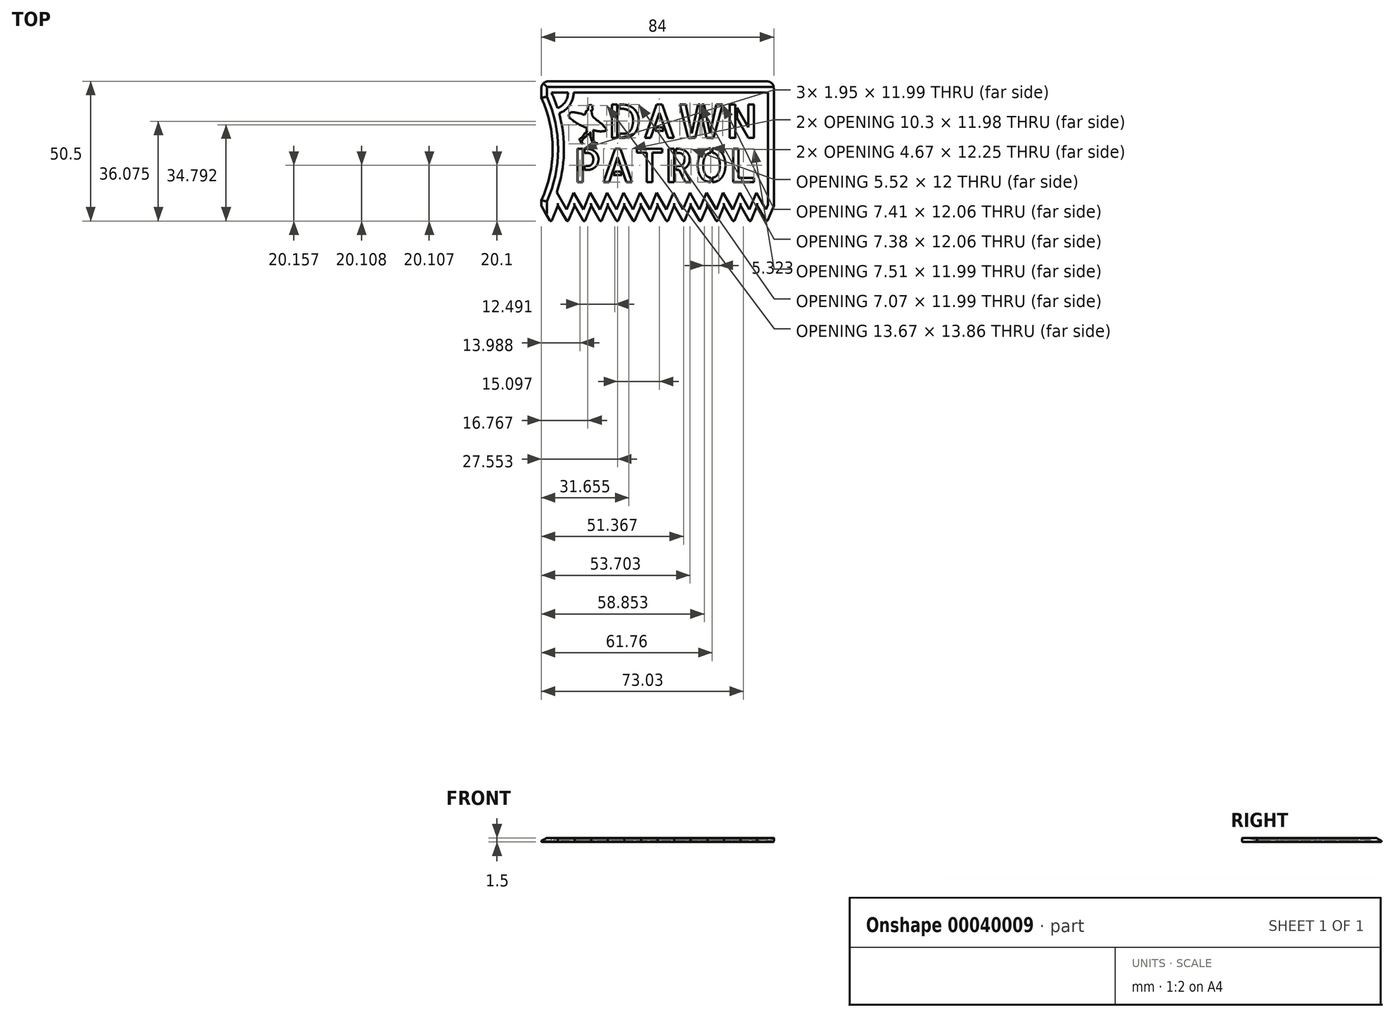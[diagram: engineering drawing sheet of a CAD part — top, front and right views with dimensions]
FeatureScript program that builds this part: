
annotation { "Feature Type Name" : "Feature", "Feature Type Description" : "" }
export const myFeature = defineFeature(function(context is Context, id is Id, definition is map)
    precondition{}
    {
        {
            assignVariable(context, id + "F0", {"name" : "t", "anyValue" : 1.5});
        }
        {
            var Q0;
            Q0=qCreatedBy(makeId("Top.planeOp"),FACE);
            var sketch = newSketch(context, id + "F1", { "sketchPlane" : qUnion([Q0])});
            skLineSegment(sketch, "E0.bottom", {"start": v(84, 51) * mm, "end": v(0, 51) * mm});
            skLineSegment(sketch, "E0.top", {"start": v(81.5, 0) * mm, "end": v(3.5, 0) * mm, "construction": true});
            skLineSegment(sketch, "E0.left", {"start": v(84, 51) * mm, "end": v(84, 6) * mm});
            skLineSegment(sketch, "E0.right", {"start": v(0, 51) * mm, "end": v(0, 6) * mm, "construction": true});
            skLineSegment(sketch, "E1", {"start": v(84, 6) * mm, "end": v(0, 6) * mm, "construction": true});
            skLineSegment(sketch, "E2", {"start": v(84, 6) * mm, "end": v(81.5, 0) * mm});
            skLineSegment(sketch, "E3", {"start": v(81.5, 0) * mm, "end": v(78, 6) * mm});
            skLineSegment(sketch, "E4.1.0.0", {"start": v(78, 6) * mm, "end": v(75.5, 0) * mm});
            skLineSegment(sketch, "E4.1.0.1", {"start": v(75.5, 0) * mm, "end": v(72, 6) * mm});
            skLineSegment(sketch, "E4.2.0.0", {"start": v(72, 6) * mm, "end": v(69.5, 0) * mm});
            skLineSegment(sketch, "E4.2.0.1", {"start": v(69.5, 0) * mm, "end": v(66, 6) * mm});
            skLineSegment(sketch, "E4.3.0.0", {"start": v(66, 6) * mm, "end": v(63.5, 0) * mm});
            skLineSegment(sketch, "E4.3.0.1", {"start": v(63.5, 0) * mm, "end": v(60, 6) * mm});
            skLineSegment(sketch, "E4.4.0.0", {"start": v(60, 6) * mm, "end": v(57.5, 0) * mm});
            skLineSegment(sketch, "E4.4.0.1", {"start": v(57.5, 0) * mm, "end": v(54, 6) * mm});
            skLineSegment(sketch, "E4.5.0.0", {"start": v(54, 6) * mm, "end": v(51.5, 0) * mm});
            skLineSegment(sketch, "E4.5.0.1", {"start": v(51.5, 0) * mm, "end": v(48, 6) * mm});
            skLineSegment(sketch, "E4.6.0.0", {"start": v(48, 6) * mm, "end": v(45.5, 0) * mm});
            skLineSegment(sketch, "E4.6.0.1", {"start": v(45.5, 0) * mm, "end": v(42, 6) * mm});
            skLineSegment(sketch, "E4.7.0.0", {"start": v(42, 6) * mm, "end": v(39.5, 0) * mm});
            skLineSegment(sketch, "E4.7.0.1", {"start": v(39.5, 0) * mm, "end": v(36, 6) * mm});
            skLineSegment(sketch, "E4.8.0.0", {"start": v(36, 6) * mm, "end": v(33.5, 0) * mm});
            skLineSegment(sketch, "E4.8.0.1", {"start": v(33.5, 0) * mm, "end": v(30, 6) * mm});
            skLineSegment(sketch, "E4.9.0.0", {"start": v(30, 6) * mm, "end": v(27.5, 0) * mm});
            skLineSegment(sketch, "E4.9.0.1", {"start": v(27.5, 0) * mm, "end": v(24, 6) * mm});
            skLineSegment(sketch, "E4.10.0.0", {"start": v(24, 6) * mm, "end": v(21.5, 0) * mm});
            skLineSegment(sketch, "E4.10.0.1", {"start": v(21.5, 0) * mm, "end": v(18, 6) * mm});
            skLineSegment(sketch, "E4.11.0.0", {"start": v(18, 6) * mm, "end": v(15.5, 0) * mm});
            skLineSegment(sketch, "E4.11.0.1", {"start": v(15.5, 0) * mm, "end": v(12, 6) * mm});
            skLineSegment(sketch, "E4.12.0.0", {"start": v(12, 6) * mm, "end": v(9.5, 0) * mm});
            skLineSegment(sketch, "E4.12.0.1", {"start": v(9.5, 0) * mm, "end": v(6, 6) * mm});
            skLineSegment(sketch, "E4.13.0.0", {"start": v(6, 6) * mm, "end": v(3.5, 0) * mm});
            skLineSegment(sketch, "E4.13.0.1", {"start": v(3.5, 0) * mm, "end": v(0, 6) * mm});
            skLineSegment(sketch, "E4.direction1", {"start": v(84, 6) * mm, "end": v(78, 6) * mm, "construction": true});
            skLineSegment(sketch, "E5", {"start": v(0, 6) * mm, "end": v(0, 8) * mm});
            skArc(sketch, "E6", {"start": v(0, 8) * mm, "mid": v(4.07, 26.5) * mm, "end": v(0, 45) * mm});
            skLineSegment(sketch, "E7", {"start": v(0, 45) * mm, "end": v(0, 51) * mm});
            skLineSegment(sketch, "E8", {"start": v(0, 6) * mm, "end": v(0, 0) * mm, "construction": true});
            skSolve(sketch);
        }
        {
            var Q0;
            Q0=qSketchRegion(id+"F1",true);
            extrude(context, id + "F2", {"entities" : qUnion([Q0]), "depth" : (getVariable(context, 't')) * mm});
        }
        {
            var Q0;
            Q0=makeQuery(id+"F2.opExtrude","CAP_EDGE",EDGE,{"disambiguationData":[OSD([sQuery(id+"F1.wireOp",EDGE,"E5")])],"isStart":false});
            var Q1;
            Q1=makeQuery(id+"F2.opExtrude","CAP_EDGE",EDGE,{"disambiguationData":[OSD([sQuery(id+"F1.wireOp",EDGE,"E6")])],"isStart":false});
            var Q2;
            Q2=makeQuery(id+"F2.opExtrude","CAP_EDGE",EDGE,{"disambiguationData":[OSD([sQuery(id+"F1.wireOp",EDGE,"E0.bottom")])],"isStart":false});
            var Q3;
            Q3=makeQuery(id+"F2.opExtrude","CAP_EDGE",EDGE,{"disambiguationData":[OSD([sQuery(id+"F1.wireOp",EDGE,"E7")])],"isStart":false});
            chamfer(context, id + "F3", {"entities" : qUnion([Q0, Q1, Q2, Q3]), "chamferType" : ChamferType.TWO_OFFSETS, "width1" : (getVariable(context, 't') * 2.2 / 3) * mm, "oppositeDirection" : false, "width2" : (getVariable(context, 't') * 4 / 3) * mm, "tangentPropagation" : true});
        }
        {
            var Q0;
            Q0=makeQuery(id+"F2.opExtrude","SWEPT_EDGE",EDGE,{"disambiguationData":[OSD([sQuery(id+"F1.wireOp",EDGE,"E0.bottom"),sQuery(id+"F1.wireOp",EDGE,"E7")])]});
            var Q1;
            Q1=makeQuery(id+"F2.opExtrude","SWEPT_EDGE",EDGE,{"disambiguationData":[OSD([sQuery(id+"F1.wireOp",EDGE,"E0.bottom"),sQuery(id+"F1.wireOp",EDGE,"E0.left")])]});
            fillet(context, id + "F4", {"entities" : qUnion([Q0, Q1]), "radius" : 2.5 * mm, "tangentPropagation" : true, "allowEdgeOverflow" : false});
        }
        {
            var Q0;
            Q0=makeQuery(id+"F2.opExtrude","CAP_FACE",FACE,{"disambiguationData":[OSD([sQuery(id+"F1.wireOp",EDGE,"E0.bottom"),sQuery(id+"F1.wireOp",EDGE,"E0.left"),sQuery(id+"F1.wireOp",EDGE,"E2"),sQuery(id+"F1.wireOp",EDGE,"E3"),sQuery(id+"F1.wireOp",EDGE,"E4.1.0.0"),sQuery(id+"F1.wireOp",EDGE,"E4.1.0.1"),sQuery(id+"F1.wireOp",EDGE,"E4.2.0.0"),sQuery(id+"F1.wireOp",EDGE,"E4.2.0.1"),sQuery(id+"F1.wireOp",EDGE,"E4.3.0.0"),sQuery(id+"F1.wireOp",EDGE,"E4.3.0.1"),sQuery(id+"F1.wireOp",EDGE,"E4.4.0.0"),sQuery(id+"F1.wireOp",EDGE,"E4.4.0.1"),sQuery(id+"F1.wireOp",EDGE,"E4.5.0.0"),sQuery(id+"F1.wireOp",EDGE,"E4.5.0.1"),sQuery(id+"F1.wireOp",EDGE,"E4.6.0.0"),sQuery(id+"F1.wireOp",EDGE,"E4.6.0.1"),sQuery(id+"F1.wireOp",EDGE,"E4.7.0.0"),sQuery(id+"F1.wireOp",EDGE,"E4.7.0.1"),sQuery(id+"F1.wireOp",EDGE,"E4.8.0.0"),sQuery(id+"F1.wireOp",EDGE,"E4.8.0.1"),sQuery(id+"F1.wireOp",EDGE,"E4.9.0.0"),sQuery(id+"F1.wireOp",EDGE,"E4.9.0.1"),sQuery(id+"F1.wireOp",EDGE,"E4.10.0.0"),sQuery(id+"F1.wireOp",EDGE,"E4.10.0.1"),sQuery(id+"F1.wireOp",EDGE,"E4.11.0.0"),sQuery(id+"F1.wireOp",EDGE,"E4.11.0.1"),sQuery(id+"F1.wireOp",EDGE,"E4.12.0.0"),sQuery(id+"F1.wireOp",EDGE,"E4.12.0.1"),sQuery(id+"F1.wireOp",EDGE,"E4.13.0.0"),sQuery(id+"F1.wireOp",EDGE,"E4.13.0.1"),sQuery(id+"F1.wireOp",EDGE,"E5"),sQuery(id+"F1.wireOp",EDGE,"E6"),sQuery(id+"F1.wireOp",EDGE,"E7")])],"isStart":false});
            var sketch = newSketch(context, id + "F5", { "sketchPlane" : qUnion([Q0])});
            skLineSegment(sketch, "E9.0", {"start": v(81.9, 6.42) * mm, "end": v(81.9, 46.9) * mm});
            skLineSegment(sketch, "E9.1", {"start": v(81.19, 4.7) * mm, "end": v(81.9, 6.42) * mm});
            skLineSegment(sketch, "E9.2", {"start": v(77.69, 10.7) * mm, "end": v(81.19, 4.7) * mm});
            skLineSegment(sketch, "E9.3", {"start": v(75.19, 4.7) * mm, "end": v(77.69, 10.7) * mm});
            skLineSegment(sketch, "E9.4", {"start": v(71.69, 10.7) * mm, "end": v(75.19, 4.7) * mm});
            skLineSegment(sketch, "E9.5", {"start": v(69.19, 4.7) * mm, "end": v(71.69, 10.7) * mm});
            skLineSegment(sketch, "E9.6", {"start": v(65.69, 10.7) * mm, "end": v(69.19, 4.7) * mm});
            skLineSegment(sketch, "E9.7", {"start": v(81.9, 46.9) * mm, "end": v(3.64, 46.9) * mm});
            skArc(sketch, "E9.8", {"start": v(3.64, 46.9) * mm, "mid": v(8.1, 29.09) * mm, "end": v(5.57, 10.9) * mm});
            skLineSegment(sketch, "E9.9", {"start": v(5.57, 10.9) * mm, "end": v(9.19, 4.7) * mm});
            skLineSegment(sketch, "E9.10", {"start": v(9.19, 4.7) * mm, "end": v(11.69, 10.7) * mm});
            skLineSegment(sketch, "E9.11", {"start": v(11.69, 10.7) * mm, "end": v(15.19, 4.7) * mm});
            skLineSegment(sketch, "E9.12", {"start": v(15.19, 4.7) * mm, "end": v(17.69, 10.7) * mm});
            skLineSegment(sketch, "E9.13", {"start": v(17.69, 10.7) * mm, "end": v(21.19, 4.7) * mm});
            skLineSegment(sketch, "E9.14", {"start": v(21.19, 4.7) * mm, "end": v(23.69, 10.7) * mm});
            skLineSegment(sketch, "E9.15", {"start": v(23.69, 10.7) * mm, "end": v(27.19, 4.7) * mm});
            skLineSegment(sketch, "E9.16", {"start": v(27.19, 4.7) * mm, "end": v(29.69, 10.7) * mm});
            skLineSegment(sketch, "E9.17", {"start": v(29.69, 10.7) * mm, "end": v(33.19, 4.7) * mm});
            skLineSegment(sketch, "E9.18", {"start": v(33.19, 4.7) * mm, "end": v(35.69, 10.7) * mm});
            skLineSegment(sketch, "E9.19", {"start": v(35.69, 10.7) * mm, "end": v(39.19, 4.7) * mm});
            skLineSegment(sketch, "E9.20", {"start": v(39.19, 4.7) * mm, "end": v(41.69, 10.7) * mm});
            skLineSegment(sketch, "E9.21", {"start": v(41.69, 10.7) * mm, "end": v(45.19, 4.7) * mm});
            skLineSegment(sketch, "E9.22", {"start": v(45.19, 4.7) * mm, "end": v(47.69, 10.7) * mm});
            skLineSegment(sketch, "E9.23", {"start": v(47.69, 10.7) * mm, "end": v(51.19, 4.7) * mm});
            skLineSegment(sketch, "E9.24", {"start": v(51.19, 4.7) * mm, "end": v(53.69, 10.7) * mm});
            skLineSegment(sketch, "E9.25", {"start": v(53.69, 10.7) * mm, "end": v(57.19, 4.7) * mm});
            skLineSegment(sketch, "E9.26", {"start": v(57.19, 4.7) * mm, "end": v(59.69, 10.7) * mm});
            skLineSegment(sketch, "E9.27", {"start": v(59.69, 10.7) * mm, "end": v(63.19, 4.7) * mm});
            skLineSegment(sketch, "E9.28", {"start": v(63.19, 4.7) * mm, "end": v(65.69, 10.7) * mm});
            skSolve(sketch);
        }
        {
            var Q0;
            Q0=makeQuery(id+"F5.imprint","IMPRINT",FACE,{"disambiguationData":[TD([[makeQuery(id+"F5.imprint","IMPRINT",EDGE,{"derivedFrom":sQuery(id+"F5.wireOp",EDGE,"E9.0")}),1.0]])]});
            extrude(context, id + "F6", {"entities" : qUnion([Q0]), "operationType" : NewBodyOperationType.REMOVE, "oppositeDirection" : true, "depth" : (getVariable(context, 't') * 2 / 5) * mm});
        }
        {
            var Q0;
            Q0=makeQuery(id+"F2.opExtrude","CAP_FACE",FACE,{"disambiguationData":[OSD([sQuery(id+"F1.wireOp",EDGE,"E0.bottom"),sQuery(id+"F1.wireOp",EDGE,"E0.left"),sQuery(id+"F1.wireOp",EDGE,"E2"),sQuery(id+"F1.wireOp",EDGE,"E3"),sQuery(id+"F1.wireOp",EDGE,"E4.1.0.0"),sQuery(id+"F1.wireOp",EDGE,"E4.1.0.1"),sQuery(id+"F1.wireOp",EDGE,"E4.2.0.0"),sQuery(id+"F1.wireOp",EDGE,"E4.2.0.1"),sQuery(id+"F1.wireOp",EDGE,"E4.3.0.0"),sQuery(id+"F1.wireOp",EDGE,"E4.3.0.1"),sQuery(id+"F1.wireOp",EDGE,"E4.4.0.0"),sQuery(id+"F1.wireOp",EDGE,"E4.4.0.1"),sQuery(id+"F1.wireOp",EDGE,"E4.5.0.0"),sQuery(id+"F1.wireOp",EDGE,"E4.5.0.1"),sQuery(id+"F1.wireOp",EDGE,"E4.6.0.0"),sQuery(id+"F1.wireOp",EDGE,"E4.6.0.1"),sQuery(id+"F1.wireOp",EDGE,"E4.7.0.0"),sQuery(id+"F1.wireOp",EDGE,"E4.7.0.1"),sQuery(id+"F1.wireOp",EDGE,"E4.8.0.0"),sQuery(id+"F1.wireOp",EDGE,"E4.8.0.1"),sQuery(id+"F1.wireOp",EDGE,"E4.9.0.0"),sQuery(id+"F1.wireOp",EDGE,"E4.9.0.1"),sQuery(id+"F1.wireOp",EDGE,"E4.10.0.0"),sQuery(id+"F1.wireOp",EDGE,"E4.10.0.1"),sQuery(id+"F1.wireOp",EDGE,"E4.11.0.0"),sQuery(id+"F1.wireOp",EDGE,"E4.11.0.1"),sQuery(id+"F1.wireOp",EDGE,"E4.12.0.0"),sQuery(id+"F1.wireOp",EDGE,"E4.12.0.1"),sQuery(id+"F1.wireOp",EDGE,"E4.13.0.0"),sQuery(id+"F1.wireOp",EDGE,"E4.13.0.1"),sQuery(id+"F1.wireOp",EDGE,"E5"),sQuery(id+"F1.wireOp",EDGE,"E6"),sQuery(id+"F1.wireOp",EDGE,"E7")])],"isStart":true});
            var Q1;
            Q1=makeQuery(id+"F2.opExtrude","CAP_EDGE",EDGE,{"disambiguationData":[OSD([sQuery(id+"F1.wireOp",EDGE,"E4.13.0.1")])],"isStart":false});
            var Q2;
            Q2=makeQuery(id+"F2.opExtrude","CAP_EDGE",EDGE,{"disambiguationData":[OSD([sQuery(id+"F1.wireOp",EDGE,"E4.13.0.0")])],"isStart":false});
            var Q3;
            Q3=makeQuery(id+"F2.opExtrude","SWEPT_EDGE",EDGE,{"disambiguationData":[OSD([sQuery(id+"F1.wireOp",EDGE,"E4.13.0.0"),sQuery(id+"F1.wireOp",EDGE,"E4.13.0.1")])]});
            var Q4;
            Q4=makeQuery(id+"F2.opExtrude","CAP_EDGE",EDGE,{"disambiguationData":[OSD([sQuery(id+"F1.wireOp",EDGE,"E4.12.0.1")])],"isStart":false});
            var Q5;
            Q5=makeQuery(id+"F2.opExtrude","SWEPT_EDGE",EDGE,{"disambiguationData":[OSD([sQuery(id+"F1.wireOp",EDGE,"E4.12.0.0"),sQuery(id+"F1.wireOp",EDGE,"E4.12.0.1")])]});
            var Q6;
            Q6=makeQuery(id+"F2.opExtrude","CAP_EDGE",EDGE,{"disambiguationData":[OSD([sQuery(id+"F1.wireOp",EDGE,"E4.12.0.0")])],"isStart":false});
            var Q7;
            Q7=makeQuery(id+"F2.opExtrude","CAP_EDGE",EDGE,{"disambiguationData":[OSD([sQuery(id+"F1.wireOp",EDGE,"E4.11.0.1")])],"isStart":false});
            var Q8;
            Q8=makeQuery(id+"F2.opExtrude","SWEPT_EDGE",EDGE,{"disambiguationData":[OSD([sQuery(id+"F1.wireOp",EDGE,"E4.11.0.0"),sQuery(id+"F1.wireOp",EDGE,"E4.11.0.1")])]});
            var Q9;
            Q9=makeQuery(id+"F2.opExtrude","CAP_EDGE",EDGE,{"disambiguationData":[OSD([sQuery(id+"F1.wireOp",EDGE,"E4.11.0.0")])],"isStart":false});
            var Q10;
            Q10=makeQuery(id+"F2.opExtrude","CAP_EDGE",EDGE,{"disambiguationData":[OSD([sQuery(id+"F1.wireOp",EDGE,"E4.10.0.1")])],"isStart":false});
            var Q11;
            Q11=makeQuery(id+"F2.opExtrude","CAP_EDGE",EDGE,{"disambiguationData":[OSD([sQuery(id+"F1.wireOp",EDGE,"E4.10.0.0")])],"isStart":false});
            var Q12;
            Q12=makeQuery(id+"F2.opExtrude","CAP_EDGE",EDGE,{"disambiguationData":[OSD([sQuery(id+"F1.wireOp",EDGE,"E4.9.0.1")])],"isStart":false});
            var Q13;
            Q13=makeQuery(id+"F2.opExtrude","CAP_EDGE",EDGE,{"disambiguationData":[OSD([sQuery(id+"F1.wireOp",EDGE,"E4.9.0.0")])],"isStart":false});
            var Q14;
            Q14=makeQuery(id+"F2.opExtrude","CAP_EDGE",EDGE,{"disambiguationData":[OSD([sQuery(id+"F1.wireOp",EDGE,"E4.8.0.1")])],"isStart":false});
            var Q15;
            Q15=makeQuery(id+"F2.opExtrude","CAP_EDGE",EDGE,{"disambiguationData":[OSD([sQuery(id+"F1.wireOp",EDGE,"E4.8.0.0")])],"isStart":false});
            var Q16;
            Q16=makeQuery(id+"F2.opExtrude","CAP_EDGE",EDGE,{"disambiguationData":[OSD([sQuery(id+"F1.wireOp",EDGE,"E4.7.0.1")])],"isStart":false});
            var Q17;
            Q17=makeQuery(id+"F2.opExtrude","CAP_EDGE",EDGE,{"disambiguationData":[OSD([sQuery(id+"F1.wireOp",EDGE,"E4.7.0.0")])],"isStart":false});
            var Q18;
            Q18=makeQuery(id+"F2.opExtrude","CAP_EDGE",EDGE,{"disambiguationData":[OSD([sQuery(id+"F1.wireOp",EDGE,"E4.6.0.1")])],"isStart":false});
            var Q19;
            Q19=makeQuery(id+"F2.opExtrude","CAP_EDGE",EDGE,{"disambiguationData":[OSD([sQuery(id+"F1.wireOp",EDGE,"E4.6.0.0")])],"isStart":false});
            var Q20;
            Q20=makeQuery(id+"F2.opExtrude","CAP_EDGE",EDGE,{"disambiguationData":[OSD([sQuery(id+"F1.wireOp",EDGE,"E4.5.0.1")])],"isStart":false});
            var Q21;
            Q21=makeQuery(id+"F2.opExtrude","CAP_EDGE",EDGE,{"disambiguationData":[OSD([sQuery(id+"F1.wireOp",EDGE,"E4.5.0.0")])],"isStart":false});
            var Q22;
            Q22=makeQuery(id+"F2.opExtrude","CAP_EDGE",EDGE,{"disambiguationData":[OSD([sQuery(id+"F1.wireOp",EDGE,"E4.4.0.1")])],"isStart":false});
            var Q23;
            Q23=makeQuery(id+"F2.opExtrude","CAP_EDGE",EDGE,{"disambiguationData":[OSD([sQuery(id+"F1.wireOp",EDGE,"E4.4.0.0")])],"isStart":false});
            var Q24;
            Q24=makeQuery(id+"F2.opExtrude","CAP_EDGE",EDGE,{"disambiguationData":[OSD([sQuery(id+"F1.wireOp",EDGE,"E4.3.0.1")])],"isStart":false});
            var Q25;
            Q25=makeQuery(id+"F2.opExtrude","CAP_EDGE",EDGE,{"disambiguationData":[OSD([sQuery(id+"F1.wireOp",EDGE,"E4.3.0.0")])],"isStart":false});
            var Q26;
            Q26=makeQuery(id+"F2.opExtrude","CAP_EDGE",EDGE,{"disambiguationData":[OSD([sQuery(id+"F1.wireOp",EDGE,"E4.2.0.1")])],"isStart":false});
            var Q27;
            Q27=makeQuery(id+"F2.opExtrude","CAP_EDGE",EDGE,{"disambiguationData":[OSD([sQuery(id+"F1.wireOp",EDGE,"E4.2.0.0")])],"isStart":false});
            var Q28;
            Q28=makeQuery(id+"F2.opExtrude","CAP_EDGE",EDGE,{"disambiguationData":[OSD([sQuery(id+"F1.wireOp",EDGE,"E4.1.0.1")])],"isStart":false});
            var Q29;
            Q29=makeQuery(id+"F2.opExtrude","CAP_EDGE",EDGE,{"disambiguationData":[OSD([sQuery(id+"F1.wireOp",EDGE,"E4.1.0.0")])],"isStart":false});
            var Q30;
            Q30=makeQuery(id+"F2.opExtrude","CAP_EDGE",EDGE,{"disambiguationData":[OSD([sQuery(id+"F1.wireOp",EDGE,"E3")])],"isStart":false});
            var Q31;
            Q31=makeQuery(id+"F2.opExtrude","SWEPT_EDGE",EDGE,{"disambiguationData":[OSD([sQuery(id+"F1.wireOp",EDGE,"E2"),sQuery(id+"F1.wireOp",EDGE,"E3")])]});
            var Q32;
            Q32=makeQuery(id+"F2.opExtrude","CAP_EDGE",EDGE,{"disambiguationData":[OSD([sQuery(id+"F1.wireOp",EDGE,"E2")])],"isStart":false});
            var Q33;
            Q33=makeQuery(id+"F2.opExtrude","SWEPT_EDGE",EDGE,{"disambiguationData":[OSD([sQuery(id+"F1.wireOp",EDGE,"E4.1.0.0"),sQuery(id+"F1.wireOp",EDGE,"E4.1.0.1")])]});
            var Q34;
            Q34=makeQuery(id+"F2.opExtrude","SWEPT_EDGE",EDGE,{"disambiguationData":[OSD([sQuery(id+"F1.wireOp",EDGE,"E4.2.0.0"),sQuery(id+"F1.wireOp",EDGE,"E4.2.0.1")])]});
            var Q35;
            Q35=makeQuery(id+"F2.opExtrude","SWEPT_EDGE",EDGE,{"disambiguationData":[OSD([sQuery(id+"F1.wireOp",EDGE,"E4.3.0.0"),sQuery(id+"F1.wireOp",EDGE,"E4.3.0.1")])]});
            var Q36;
            Q36=makeQuery(id+"F2.opExtrude","SWEPT_EDGE",EDGE,{"disambiguationData":[OSD([sQuery(id+"F1.wireOp",EDGE,"E4.4.0.0"),sQuery(id+"F1.wireOp",EDGE,"E4.4.0.1")])]});
            var Q37;
            Q37=makeQuery(id+"F2.opExtrude","SWEPT_EDGE",EDGE,{"disambiguationData":[OSD([sQuery(id+"F1.wireOp",EDGE,"E4.5.0.0"),sQuery(id+"F1.wireOp",EDGE,"E4.5.0.1")])]});
            var Q38;
            Q38=makeQuery(id+"F2.opExtrude","SWEPT_EDGE",EDGE,{"disambiguationData":[OSD([sQuery(id+"F1.wireOp",EDGE,"E4.6.0.0"),sQuery(id+"F1.wireOp",EDGE,"E4.6.0.1")])]});
            var Q39;
            Q39=makeQuery(id+"F2.opExtrude","SWEPT_EDGE",EDGE,{"disambiguationData":[OSD([sQuery(id+"F1.wireOp",EDGE,"E4.7.0.0"),sQuery(id+"F1.wireOp",EDGE,"E4.7.0.1")])]});
            var Q40;
            Q40=makeQuery(id+"F2.opExtrude","SWEPT_EDGE",EDGE,{"disambiguationData":[OSD([sQuery(id+"F1.wireOp",EDGE,"E4.8.0.0"),sQuery(id+"F1.wireOp",EDGE,"E4.8.0.1")])]});
            var Q41;
            Q41=makeQuery(id+"F2.opExtrude","SWEPT_EDGE",EDGE,{"disambiguationData":[OSD([sQuery(id+"F1.wireOp",EDGE,"E4.9.0.0"),sQuery(id+"F1.wireOp",EDGE,"E4.9.0.1")])]});
            var Q42;
            Q42=makeQuery(id+"F2.opExtrude","SWEPT_EDGE",EDGE,{"disambiguationData":[OSD([sQuery(id+"F1.wireOp",EDGE,"E4.10.0.0"),sQuery(id+"F1.wireOp",EDGE,"E4.10.0.1")])]});
            fillet(context, id + "F7", {"entities" : qUnion([Q0, Q1, Q2, Q3, Q4, Q5, Q6, Q7, Q8, Q9, Q10, Q11, Q12, Q13, Q14, Q15, Q16, Q17, Q18, Q19, Q20, Q21, Q22, Q23, Q24, Q25, Q26, Q27, Q28, Q29, Q30, Q31, Q32, Q33, Q34, Q35, Q36, Q37, Q38, Q39, Q40, Q41, Q42]), "radius" : .4 * mm, "tangentPropagation" : true, "allowEdgeOverflow" : false});
        }
        {
            var Q0;
            Q0=makeQuery(id+"F6.boolean.opBoolean","COPY",FACE,{"derivedFrom":makeQuery(id+"F6.opExtrude","CAP_FACE",FACE,{"disambiguationData":[OSD([sQuery(id+"F5.wireOp",EDGE,"E9.0"),sQuery(id+"F5.wireOp",EDGE,"E9.1"),sQuery(id+"F5.wireOp",EDGE,"E9.2"),sQuery(id+"F5.wireOp",EDGE,"E9.3"),sQuery(id+"F5.wireOp",EDGE,"E9.4"),sQuery(id+"F5.wireOp",EDGE,"E9.5"),sQuery(id+"F5.wireOp",EDGE,"E9.6"),sQuery(id+"F5.wireOp",EDGE,"E9.7"),sQuery(id+"F5.wireOp",EDGE,"E9.8"),sQuery(id+"F5.wireOp",EDGE,"E9.9"),sQuery(id+"F5.wireOp",EDGE,"E9.10"),sQuery(id+"F5.wireOp",EDGE,"E9.11"),sQuery(id+"F5.wireOp",EDGE,"E9.12"),sQuery(id+"F5.wireOp",EDGE,"E9.13"),sQuery(id+"F5.wireOp",EDGE,"E9.14"),sQuery(id+"F5.wireOp",EDGE,"E9.15"),sQuery(id+"F5.wireOp",EDGE,"E9.16"),sQuery(id+"F5.wireOp",EDGE,"E9.17"),sQuery(id+"F5.wireOp",EDGE,"E9.18"),sQuery(id+"F5.wireOp",EDGE,"E9.19"),sQuery(id+"F5.wireOp",EDGE,"E9.20"),sQuery(id+"F5.wireOp",EDGE,"E9.21"),sQuery(id+"F5.wireOp",EDGE,"E9.22"),sQuery(id+"F5.wireOp",EDGE,"E9.23"),sQuery(id+"F5.wireOp",EDGE,"E9.24"),sQuery(id+"F5.wireOp",EDGE,"E9.25"),sQuery(id+"F5.wireOp",EDGE,"E9.26"),sQuery(id+"F5.wireOp",EDGE,"E9.27"),sQuery(id+"F5.wireOp",EDGE,"E9.28")])],"isStart":false})});
            var sketch = newSketch(context, id + "F8", { "sketchPlane" : qUnion([Q0])});
            skText(sketch, "E10", { "text": "PATROL", "fontName": "AllertaStencil-Regular.ttf"});
            skText(sketch, "E11", { "text": "DAWN", "fontName": "AllertaStencil-Regular.ttf"});
            skArc(sketch, "E12.0", {"start": v(3.64, 46.9) * mm, "mid": v(8.1, 29.09) * mm, "end": v(5.57, 10.9) * mm});
            skLineSegment(sketch, "E12.1", {"start": v(81.9, 46.9) * mm, "end": v(3.64, 46.9) * mm});
            skArc(sketch, "E13.0", {"start": v(3.64, 46.9) * mm, "mid": v(4.82, 44.14) * mm, "end": v(5.84, 41.32) * mm});
            skLineSegment(sketch, "E14", {"start": v(9.64, 46.9) * mm, "end": v(3.64, 46.9) * mm});
            skLineSegment(sketch, "E15", {"start": v(3.64, 46.9) * mm, "end": v(5.84, 41.32) * mm, "construction": true});
            skArc(sketch, "E16", {"start": v(5.84, 41.32) * mm, "mid": v(8.6, 43.52) * mm, "end": v(9.64, 46.9) * mm});
            const initialGuessF8  = {"E10": [0.01153, 0.01461, 1, 0, 0.012], "E11": [0.02394, 0.03061, 1, 0, 0.012]};
            skSetInitialGuess(sketch, initialGuessF8);
            skSolve(sketch);
        }
        {
            var Q0;
            Q0=qSketchRegion(id+"F8",true);
            extrude(context, id + "F9", {"entities" : qUnion([Q0]), "operationType" : NewBodyOperationType.REMOVE, "endBound" : BoundingType.THROUGH_ALL, "oppositeDirection" : true, "depth" : 25 * mm});
        }
        {
            var Q0;
            Q0=makeQuery(id+"F6.boolean.opBoolean","COPY",FACE,{"derivedFrom":makeQuery(id+"F6.opExtrude","CAP_FACE",FACE,{"disambiguationData":[OSD([sQuery(id+"F5.wireOp",EDGE,"E9.0"),sQuery(id+"F5.wireOp",EDGE,"E9.1"),sQuery(id+"F5.wireOp",EDGE,"E9.2"),sQuery(id+"F5.wireOp",EDGE,"E9.3"),sQuery(id+"F5.wireOp",EDGE,"E9.4"),sQuery(id+"F5.wireOp",EDGE,"E9.5"),sQuery(id+"F5.wireOp",EDGE,"E9.6"),sQuery(id+"F5.wireOp",EDGE,"E9.7"),sQuery(id+"F5.wireOp",EDGE,"E9.8"),sQuery(id+"F5.wireOp",EDGE,"E9.9"),sQuery(id+"F5.wireOp",EDGE,"E9.10"),sQuery(id+"F5.wireOp",EDGE,"E9.11"),sQuery(id+"F5.wireOp",EDGE,"E9.12"),sQuery(id+"F5.wireOp",EDGE,"E9.13"),sQuery(id+"F5.wireOp",EDGE,"E9.14"),sQuery(id+"F5.wireOp",EDGE,"E9.15"),sQuery(id+"F5.wireOp",EDGE,"E9.16"),sQuery(id+"F5.wireOp",EDGE,"E9.17"),sQuery(id+"F5.wireOp",EDGE,"E9.18"),sQuery(id+"F5.wireOp",EDGE,"E9.19"),sQuery(id+"F5.wireOp",EDGE,"E9.20"),sQuery(id+"F5.wireOp",EDGE,"E9.21"),sQuery(id+"F5.wireOp",EDGE,"E9.22"),sQuery(id+"F5.wireOp",EDGE,"E9.23"),sQuery(id+"F5.wireOp",EDGE,"E9.24"),sQuery(id+"F5.wireOp",EDGE,"E9.25"),sQuery(id+"F5.wireOp",EDGE,"E9.26"),sQuery(id+"F5.wireOp",EDGE,"E9.27"),sQuery(id+"F5.wireOp",EDGE,"E9.28")])],"isStart":false})});
            var sketch = newSketch(context, id + "F10", { "sketchPlane" : qUnion([Q0])});
            skArc(sketch, "E17.0", {"start": v(5.84, 41.32) * mm, "mid": v(8.6, 43.52) * mm, "end": v(9.64, 46.9) * mm});
            skArc(sketch, "E18.0", {"start": v(6.57, 39.46) * mm, "mid": v(10.25, 42.4) * mm, "end": v(11.64, 46.9) * mm});
            skLineSegment(sketch, "E19.0", {"start": v(76.9, 41.9) * mm, "end": v(13.44, 41.9) * mm});
            skLineSegment(sketch, "E19.1", {"start": v(76.9, 21.82) * mm, "end": v(76.9, 41.9) * mm});
            skLineSegment(sketch, "E19.2", {"start": v(74.44, 15.91) * mm, "end": v(76.9, 21.82) * mm});
            skLineSegment(sketch, "E19.3", {"start": v(34.94, 21.91) * mm, "end": v(38.44, 15.91) * mm});
            skLineSegment(sketch, "E19.4", {"start": v(32.44, 15.91) * mm, "end": v(34.94, 21.91) * mm});
            skLineSegment(sketch, "E19.5", {"start": v(28.94, 21.91) * mm, "end": v(32.44, 15.91) * mm});
            skLineSegment(sketch, "E19.6", {"start": v(26.44, 15.91) * mm, "end": v(28.94, 21.91) * mm});
            skLineSegment(sketch, "E19.7", {"start": v(22.94, 21.91) * mm, "end": v(26.44, 15.91) * mm});
            skLineSegment(sketch, "E19.8", {"start": v(20.44, 15.91) * mm, "end": v(22.94, 21.91) * mm});
            skArc(sketch, "E19.9", {"start": v(11.6, 39.31) * mm, "mid": v(13.1, 29.2) * mm, "end": v(12.64, 19) * mm});
            skLineSegment(sketch, "E19.10", {"start": v(12.64, 19) * mm, "end": v(14.44, 15.91) * mm});
            skLineSegment(sketch, "E19.11", {"start": v(14.44, 15.91) * mm, "end": v(16.94, 21.91) * mm});
            skLineSegment(sketch, "E19.12", {"start": v(16.94, 21.91) * mm, "end": v(20.44, 15.91) * mm});
            skLineSegment(sketch, "E19.13", {"start": v(38.44, 15.91) * mm, "end": v(40.94, 21.91) * mm});
            skLineSegment(sketch, "E19.14", {"start": v(40.94, 21.91) * mm, "end": v(44.44, 15.91) * mm});
            skLineSegment(sketch, "E19.15", {"start": v(44.44, 15.91) * mm, "end": v(46.94, 21.91) * mm});
            skArc(sketch, "E19.16", {"start": v(13.44, 41.9) * mm, "mid": v(12.61, 40.54) * mm, "end": v(11.6, 39.31) * mm});
            skLineSegment(sketch, "E19.17", {"start": v(46.94, 21.91) * mm, "end": v(50.44, 15.91) * mm});
            skLineSegment(sketch, "E19.18", {"start": v(50.44, 15.91) * mm, "end": v(52.94, 21.91) * mm});
            skLineSegment(sketch, "E19.19", {"start": v(52.94, 21.91) * mm, "end": v(56.44, 15.91) * mm});
            skLineSegment(sketch, "E19.20", {"start": v(56.44, 15.91) * mm, "end": v(58.94, 21.91) * mm});
            skLineSegment(sketch, "E19.21", {"start": v(58.94, 21.91) * mm, "end": v(62.44, 15.91) * mm});
            skLineSegment(sketch, "E19.22", {"start": v(62.44, 15.91) * mm, "end": v(64.94, 21.91) * mm});
            skLineSegment(sketch, "E19.23", {"start": v(64.94, 21.91) * mm, "end": v(68.44, 15.91) * mm});
            skLineSegment(sketch, "E19.24", {"start": v(68.44, 15.91) * mm, "end": v(70.94, 21.91) * mm});
            skLineSegment(sketch, "E19.25", {"start": v(70.94, 21.91) * mm, "end": v(74.44, 15.91) * mm});
            skLineSegment(sketch, "E20", {"start": v(9.64, 46.9) * mm, "end": v(11.64, 46.9) * mm});
            skArc(sketch, "E21", {"start": v(6.57, 39.46) * mm, "mid": v(6.5, 39.43) * mm, "end": v(6.41, 39.4) * mm});
            skArc(sketch, "E22.0", {"start": v(5.84, 41.32) * mm, "mid": v(8.17, 26.09) * mm, "end": v(5.57, 10.9) * mm});
            skArc(sketch, "E23.0", {"start": v(5.84, 41.32) * mm, "mid": v(6.13, 40.36) * mm, "end": v(6.41, 39.4) * mm});
            skArc(sketch, "E24", {"start": v(6.41, 39.4) * mm, "mid": v(8.15, 25.08) * mm, "end": v(5.57, 10.9) * mm});
            skSolve(sketch);
        }
        {
            var Q0;
            Q0=makeQuery(id+"F10.imprint","IMPRINT",FACE,{"disambiguationData":[TD([[makeQuery(id+"F10.imprint","IMPRINT",EDGE,{"derivedFrom":sQuery(id+"F10.wireOp",EDGE,"E17.0")}),-1.0]])]});
            var Q1;
            Q1=makeQuery(id+"F2.opExtrude","CAP_FACE",FACE,{"disambiguationData":[OSD([sQuery(id+"F1.wireOp",EDGE,"E0.bottom"),sQuery(id+"F1.wireOp",EDGE,"E0.left"),sQuery(id+"F1.wireOp",EDGE,"E2"),sQuery(id+"F1.wireOp",EDGE,"E3"),sQuery(id+"F1.wireOp",EDGE,"E4.1.0.0"),sQuery(id+"F1.wireOp",EDGE,"E4.1.0.1"),sQuery(id+"F1.wireOp",EDGE,"E4.2.0.0"),sQuery(id+"F1.wireOp",EDGE,"E4.2.0.1"),sQuery(id+"F1.wireOp",EDGE,"E4.3.0.0"),sQuery(id+"F1.wireOp",EDGE,"E4.3.0.1"),sQuery(id+"F1.wireOp",EDGE,"E4.4.0.0"),sQuery(id+"F1.wireOp",EDGE,"E4.4.0.1"),sQuery(id+"F1.wireOp",EDGE,"E4.5.0.0"),sQuery(id+"F1.wireOp",EDGE,"E4.5.0.1"),sQuery(id+"F1.wireOp",EDGE,"E4.6.0.0"),sQuery(id+"F1.wireOp",EDGE,"E4.6.0.1"),sQuery(id+"F1.wireOp",EDGE,"E4.7.0.0"),sQuery(id+"F1.wireOp",EDGE,"E4.7.0.1"),sQuery(id+"F1.wireOp",EDGE,"E4.8.0.0"),sQuery(id+"F1.wireOp",EDGE,"E4.8.0.1"),sQuery(id+"F1.wireOp",EDGE,"E4.9.0.0"),sQuery(id+"F1.wireOp",EDGE,"E4.9.0.1"),sQuery(id+"F1.wireOp",EDGE,"E4.10.0.0"),sQuery(id+"F1.wireOp",EDGE,"E4.10.0.1"),sQuery(id+"F1.wireOp",EDGE,"E4.11.0.0"),sQuery(id+"F1.wireOp",EDGE,"E4.11.0.1"),sQuery(id+"F1.wireOp",EDGE,"E4.12.0.0"),sQuery(id+"F1.wireOp",EDGE,"E4.12.0.1"),sQuery(id+"F1.wireOp",EDGE,"E4.13.0.0"),sQuery(id+"F1.wireOp",EDGE,"E4.13.0.1"),sQuery(id+"F1.wireOp",EDGE,"E5"),sQuery(id+"F1.wireOp",EDGE,"E6"),sQuery(id+"F1.wireOp",EDGE,"E7")])],"isStart":false});
            extrude(context, id + "F11", {"entities" : qUnion([Q0]), "operationType" : NewBodyOperationType.ADD, "endBound" : BoundingType.UP_TO_SURFACE, "endBoundEntityFace" : qUnion([Q1]), "depth" : 25 * mm});
        }
        {
            var Q0;
            Q0=makeQuery(id+"F6.boolean.opBoolean","COPY",FACE,{"derivedFrom":makeQuery(id+"F6.opExtrude","CAP_FACE",FACE,{"disambiguationData":[OSD([sQuery(id+"F5.wireOp",EDGE,"E9.0"),sQuery(id+"F5.wireOp",EDGE,"E9.1"),sQuery(id+"F5.wireOp",EDGE,"E9.2"),sQuery(id+"F5.wireOp",EDGE,"E9.3"),sQuery(id+"F5.wireOp",EDGE,"E9.4"),sQuery(id+"F5.wireOp",EDGE,"E9.5"),sQuery(id+"F5.wireOp",EDGE,"E9.6"),sQuery(id+"F5.wireOp",EDGE,"E9.7"),sQuery(id+"F5.wireOp",EDGE,"E9.8"),sQuery(id+"F5.wireOp",EDGE,"E9.9"),sQuery(id+"F5.wireOp",EDGE,"E9.10"),sQuery(id+"F5.wireOp",EDGE,"E9.11"),sQuery(id+"F5.wireOp",EDGE,"E9.12"),sQuery(id+"F5.wireOp",EDGE,"E9.13"),sQuery(id+"F5.wireOp",EDGE,"E9.14"),sQuery(id+"F5.wireOp",EDGE,"E9.15"),sQuery(id+"F5.wireOp",EDGE,"E9.16"),sQuery(id+"F5.wireOp",EDGE,"E9.17"),sQuery(id+"F5.wireOp",EDGE,"E9.18"),sQuery(id+"F5.wireOp",EDGE,"E9.19"),sQuery(id+"F5.wireOp",EDGE,"E9.20"),sQuery(id+"F5.wireOp",EDGE,"E9.21"),sQuery(id+"F5.wireOp",EDGE,"E9.22"),sQuery(id+"F5.wireOp",EDGE,"E9.23"),sQuery(id+"F5.wireOp",EDGE,"E9.24"),sQuery(id+"F5.wireOp",EDGE,"E9.25"),sQuery(id+"F5.wireOp",EDGE,"E9.26"),sQuery(id+"F5.wireOp",EDGE,"E9.27"),sQuery(id+"F5.wireOp",EDGE,"E9.28")])],"isStart":false})});
            var sketch = newSketch(context, id + "F12", { "sketchPlane" : qUnion([Q0])});
            skLineSegment(sketch, "E25", {"start": v(9.88, 39.16) * mm, "end": v(23.9, 33.13) * mm, "construction": true});
            skFitSpline(sketch, "E26", {"points": [v(16.33, 34.19) * mm, v(13.72, 35.36) * mm, v(11.75, 36.56) * mm, v(10.12, 38) * mm, v(9.94, 38.54) * mm, v(10.06, 39.08) * mm], "startDerivative": vector(-8.18, 3.62) * mm, "endDerivative": vector(1.44, 4.42) * mm});
            skFitSpline(sketch, "E27", {"points": [v(17.34, 38.17) * mm, v(15.28, 38.99) * mm, v(13.05, 39.6) * mm, v(10.9, 39.8) * mm, v(10.37, 39.55) * mm, v(10.06, 39.08) * mm], "startDerivative": vector(-8.26, 3.44) * mm, "endDerivative": vector(-2.21, -4.08) * mm});
            skFitSpline(sketch, "E28", {"points": [v(16.33, 34.19) * mm, v(16.33, 33.43) * mm, v(16.5, 32.86) * mm, v(16.51, 32.6) * mm, v(16.36, 32.45) * mm, v(15.8, 32.2) * mm, v(15.34, 31.67) * mm, v(14.9, 31.06) * mm, v(14.54, 30.6) * mm, v(14.34, 30.44) * mm, v(14.03, 30.31) * mm, v(13.82, 30.23) * mm, v(13.76, 30.06) * mm, v(13.87, 29.72) * mm, v(14.03, 29.56) * mm, v(14.16, 29.44) * mm, v(14.2, 29.24) * mm, v(14.23, 28.84) * mm, v(14.39, 28.64) * mm, v(14.6, 28.53) * mm, v(14.88, 28.47) * mm, v(14.93, 28.5) * mm, v(14.94, 28.54) * mm, v(14.91, 28.62) * mm, v(14.79, 28.7) * mm, v(14.68, 28.82) * mm, v(14.66, 29.1) * mm, v(14.69, 29.41) * mm, v(14.72, 29.64) * mm, v(14.8, 29.8) * mm, v(15, 30.1) * mm, v(15.53, 30.62) * mm, v(16.12, 31.11) * mm, v(16.73, 31.55) * mm, v(17.28, 31.87) * mm, v(17.51, 32.07) * mm, v(17.6, 32.3) * mm, v(17.64, 32.49) * mm, v(17.7, 32.53) * mm, v(17.73, 32.52) * mm], "startDerivative": vector(-1.7, -19.21) * mm, "endDerivative": vector(3.01, -1.59) * mm});
            skFitSpline(sketch, "E29", {"points": [v(15.6, 38.87) * mm, v(15.86, 39.52) * mm, v(16.12, 40.04) * mm, v(16.4, 40.33) * mm, v(16.7, 40.58) * mm, v(16.91, 40.76) * mm, v(16.97, 40.88) * mm, v(16.86, 41.14) * mm, v(16.76, 41.48) * mm, v(16.8, 41.88) * mm, v(16.97, 42.2) * mm, v(17.51, 42.51) * mm, v(17.96, 42.44) * mm, v(18.28, 42.3) * mm, v(18.5, 42.08) * mm, v(18.48, 41.86) * mm, v(18.42, 41.74) * mm, v(18.48, 41.62) * mm, v(18.5, 41.47) * mm, v(18.46, 41.4) * mm, v(18.45, 41.33) * mm, v(18.53, 41.22) * mm, v(18.6, 41.1) * mm, v(18.6, 41.02) * mm, v(18.57, 40.96) * mm, v(18.45, 40.98) * mm, v(18.44, 40.92) * mm, v(18.44, 40.82) * mm, v(18.41, 40.75) * mm, v(18.36, 40.69) * mm, v(18.37, 40.6) * mm, v(18.4, 40.5) * mm, v(18.38, 40.44) * mm, v(18.3, 40.4) * mm, v(18.2, 40.37) * mm, v(18.02, 40.38) * mm, v(17.92, 40.4) * mm, v(17.86, 40.35) * mm, v(17.92, 40.25) * mm, v(18.08, 40.1) * mm, v(18.22, 39.76) * mm, v(18.23, 39.24) * mm, v(18.34, 38.75) * mm, v(18.57, 38.3) * mm, v(19.04, 37.83) * mm, v(19.44, 37.47) * mm, v(19.86, 37.18) * mm, v(20.17, 36.84) * mm, v(20.43, 36.72) * mm, v(20.75, 36.6) * mm, v(20.86, 36.4) * mm, v(20.89, 36.28) * mm], "startDerivative": vector(7.84, 19.36) * mm, "endDerivative": vector(2.4, -8.81) * mm});
            skFitSpline(sketch, "E30", {"points": [v(18.66, 33.4) * mm, v(19.32, 33.2) * mm, v(20.28, 33) * mm, v(21.23, 32.9) * mm, v(22.06, 32.94) * mm, v(22.95, 33.06) * mm, v(23.58, 33.23) * mm, v(23.6, 33.26) * mm], "startDerivative": vector(4.26, -1.27) * mm, "endDerivative": vector(0.24, 0.98) * mm});
            skFitSpline(sketch, "E31.MirrorCS", {"points": [v(20.11, 36.76) * mm, v(20.7, 36.4) * mm, v(21.5, 35.85) * mm, v(22.23, 35.24) * mm, v(22.78, 34.6) * mm, v(23.3, 33.88) * mm, v(23.61, 33.3) * mm, v(23.6, 33.26) * mm], "startDerivative": vector(3.85, -2.22) * mm, "endDerivative": vector(-0.55, -0.85) * mm});
            skFitSpline(sketch, "E32", {"points": [v(18.66, 33.4) * mm, v(18.77, 32.93) * mm, v(18.83, 32.61) * mm, v(18.81, 32.18) * mm, v(18.77, 31.55) * mm, v(18.78, 30.86) * mm, v(18.83, 30.06) * mm, v(18.96, 29.4) * mm, v(19.12, 29.1) * mm, v(19.4, 28.9) * mm, v(19.65, 28.73) * mm, v(19.95, 28.66) * mm, v(20.17, 28.64) * mm, v(20.28, 28.62) * mm, v(20.28, 28.54) * mm, v(20.23, 28.46) * mm, v(20.12, 28.4) * mm, v(19.95, 28.37) * mm, v(19.65, 28.36) * mm, v(19.2, 28.37) * mm, v(18.89, 28.38) * mm, v(18.64, 28.37) * mm, v(18.48, 28.38) * mm, v(18.4, 28.42) * mm, v(18.34, 28.55) * mm, v(18.35, 28.72) * mm, v(18.42, 28.9) * mm, v(18.42, 29.08) * mm, v(18.3, 29.4) * mm, v(18.1, 29.98) * mm, v(17.9, 30.65) * mm, v(17.76, 31.3) * mm, v(17.81, 31.88) * mm, v(17.83, 32.29) * mm, v(17.8, 32.46) * mm, v(17.73, 32.52) * mm], "startDerivative": vector(2.94, -13.83) * mm, "endDerivative": vector(-5.6, 2.93) * mm});
            skSolve(sketch);
        }
        {
            var Q0;
            Q0=makeQuery(id+"F12.imprint","IMPRINT",FACE,{"disambiguationData":[TD([[makeQuery(id+"F12.imprint","IMPRINT",EDGE,{"derivedFrom":sQuery(id+"F12.wireOp",EDGE,"E26")}),-1.0]])]});
            var Q1;
            {var subQ0=sQuery(id+"F1.wireOp",EDGE,"E7");var subQ1=sQuery(id+"F1.wireOp",EDGE,"E6");var subQ2=sQuery(id+"F1.wireOp",EDGE,"E5");var subQ3=sQuery(id+"F1.wireOp",EDGE,"E4.13.0.1");var subQ4=sQuery(id+"F1.wireOp",EDGE,"E4.13.0.0");var subQ5=sQuery(id+"F1.wireOp",EDGE,"E4.12.0.1");var subQ6=sQuery(id+"F1.wireOp",EDGE,"E4.12.0.0");var subQ7=sQuery(id+"F1.wireOp",EDGE,"E4.11.0.1");var subQ8=sQuery(id+"F1.wireOp",EDGE,"E4.11.0.0");var subQ9=sQuery(id+"F1.wireOp",EDGE,"E4.10.0.1");var subQ10=sQuery(id+"F1.wireOp",EDGE,"E4.10.0.0");var subQ11=sQuery(id+"F1.wireOp",EDGE,"E4.9.0.1");var subQ12=sQuery(id+"F1.wireOp",EDGE,"E4.9.0.0");var subQ13=sQuery(id+"F1.wireOp",EDGE,"E4.8.0.1");var subQ14=sQuery(id+"F1.wireOp",EDGE,"E4.8.0.0");var subQ15=sQuery(id+"F1.wireOp",EDGE,"E4.7.0.1");var subQ16=sQuery(id+"F1.wireOp",EDGE,"E4.7.0.0");var subQ17=sQuery(id+"F1.wireOp",EDGE,"E4.6.0.1");var subQ18=sQuery(id+"F1.wireOp",EDGE,"E4.6.0.0");var subQ19=sQuery(id+"F1.wireOp",EDGE,"E4.5.0.1");var subQ20=sQuery(id+"F1.wireOp",EDGE,"E4.5.0.0");var subQ21=sQuery(id+"F1.wireOp",EDGE,"E4.4.0.1");var subQ22=sQuery(id+"F1.wireOp",EDGE,"E4.4.0.0");var subQ23=sQuery(id+"F1.wireOp",EDGE,"E4.3.0.1");var subQ24=sQuery(id+"F1.wireOp",EDGE,"E4.3.0.0");var subQ25=sQuery(id+"F1.wireOp",EDGE,"E4.2.0.1");var subQ26=sQuery(id+"F1.wireOp",EDGE,"E4.2.0.0");var subQ27=sQuery(id+"F1.wireOp",EDGE,"E4.1.0.1");var subQ28=sQuery(id+"F1.wireOp",EDGE,"E4.1.0.0");var subQ29=sQuery(id+"F1.wireOp",EDGE,"E3");var subQ30=sQuery(id+"F1.wireOp",EDGE,"E2");var subQ31=sQuery(id+"F1.wireOp",EDGE,"E0.left");var subQ32=sQuery(id+"F1.wireOp",EDGE,"E0.bottom");Q1=makeQuery(id+"F11.boolean.opBoolean","MERGE",FACE,{"derivedFrom":[makeQuery(id+"F2.opExtrude","CAP_FACE",FACE,{"disambiguationData":[OSD([subQ32,subQ31,subQ30,subQ29,subQ28,subQ27,subQ26,subQ25,subQ24,subQ23,subQ22,subQ21,subQ20,subQ19,subQ18,subQ17,subQ16,subQ15,subQ14,subQ13,subQ12,subQ11,subQ10,subQ9,subQ8,subQ7,subQ6,subQ5,subQ4,subQ3,subQ2,subQ1,subQ0])],"isStart":false}),makeQuery(id+"F11.opExtrude","CAP_FACE",FACE,{"disambiguationData":[OSD([subQ32,subQ31,subQ30,subQ29,subQ28,subQ27,subQ26,subQ25,subQ24,subQ23,subQ22,subQ21,subQ20,subQ19,subQ18,subQ17,subQ16,subQ15,subQ14,subQ13,subQ12,subQ11,subQ10,subQ9,subQ8,subQ7,subQ6,subQ5,subQ4,subQ3,subQ2,subQ1,subQ0])],"isStart":false})]});}
            extrude(context, id + "F13", {"entities" : qUnion([Q0]), "operationType" : NewBodyOperationType.REMOVE, "endBound" : BoundingType.THROUGH_ALL, "oppositeDirection" : true, "endBoundEntityFace" : qUnion([Q1]), "depth" : 25 * mm});
        }
    });
